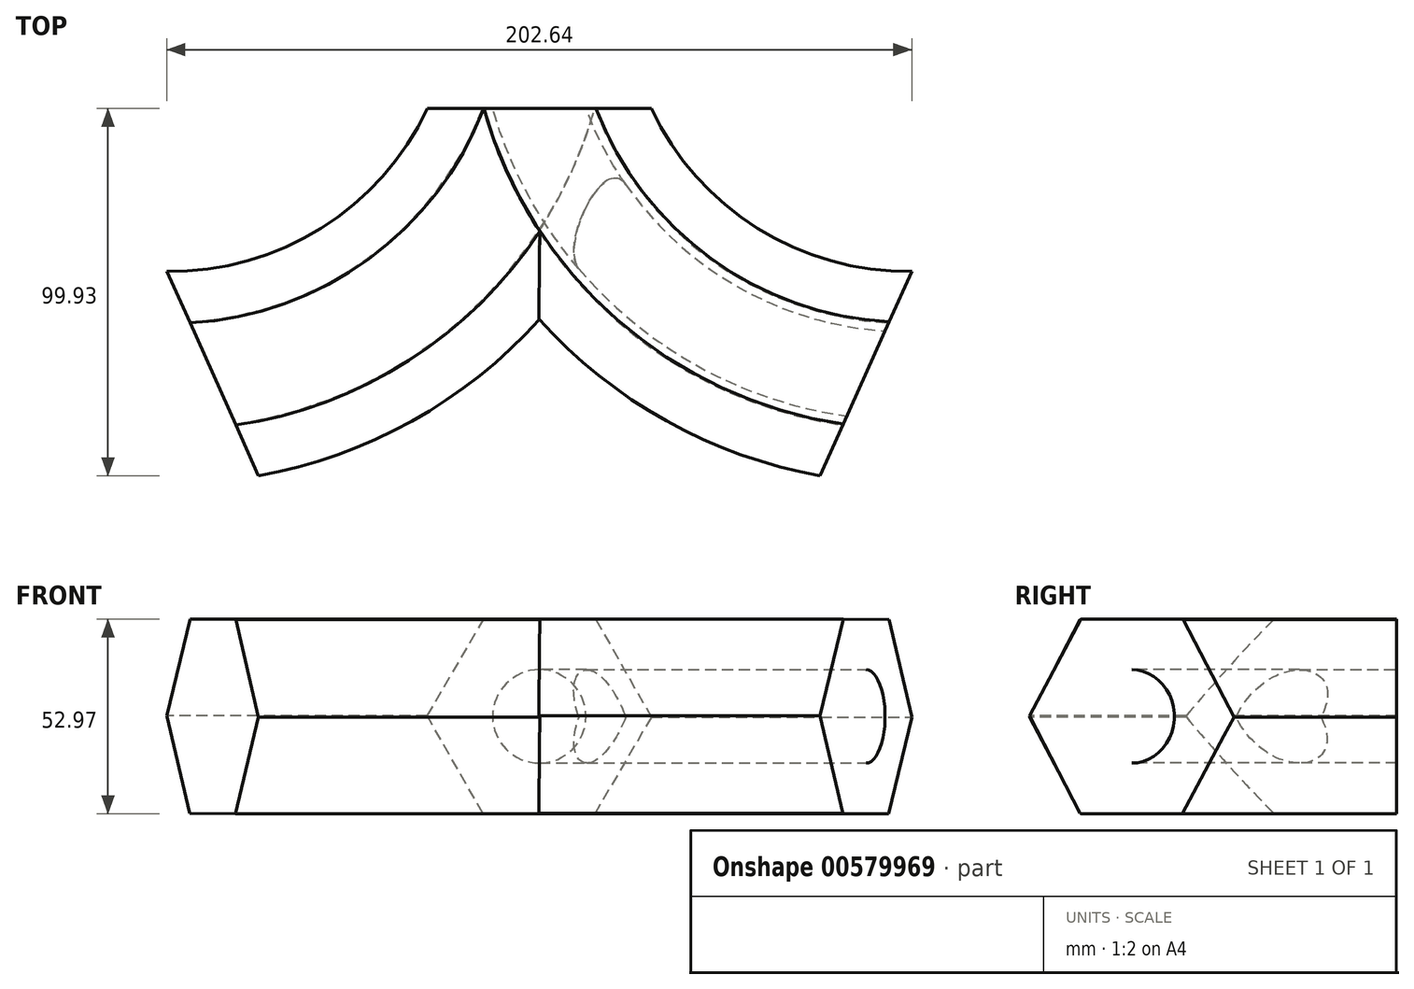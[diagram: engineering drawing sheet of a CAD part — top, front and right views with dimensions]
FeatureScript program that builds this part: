
annotation { "Feature Type Name" : "Feature", "Feature Type Description" : "" }
export const myFeature = defineFeature(function(context is Context, id is Id, definition is map)
    precondition{}
    {
        {
            var Q0;
            Q0=qCreatedBy(makeId("Front.planeOp"),FACE);
            var sketch = newSketch(context, id + "F0", { "sketchPlane" : qUnion([Q0])});
            skCircle(sketch, "E0.cCircle", {"center": v(0, 26.89) * mm, "radius": 26.4 * mm, "construction": true});
            skLineSegment(sketch, "E0.0", {"start": v(-15.4, 0.58) * mm, "end": v(-30.48, 27.07) * mm});
            skLineSegment(sketch, "E0.1", {"start": v(-30.48, 27.07) * mm, "end": v(-15.08, 53.37) * mm});
            skLineSegment(sketch, "E0.2", {"start": v(-15.08, 53.37) * mm, "end": v(15.4, 53.2) * mm});
            skLineSegment(sketch, "E0.3", {"start": v(15.4, 53.2) * mm, "end": v(30.48, 26.7) * mm});
            skLineSegment(sketch, "E0.4", {"start": v(30.48, 26.7) * mm, "end": v(15.08, 0.4) * mm});
            skLineSegment(sketch, "E0.5", {"start": v(15.08, 0.4) * mm, "end": v(-15.4, 0.58) * mm});
            skPoint(sketch, "E0.0.midPoint", {"position": v(-22.94, 13.82) * mm});
            skCircle(sketch, "E1", {"center": v(0, 26.89) * mm, "radius": 12.7 * mm});
            skSolve(sketch);
        }
        {
            var Q0;
            Q0=qCreatedBy(makeId("Top.planeOp"),FACE);
            var sketch = newSketch(context, id + "F1", { "sketchPlane" : qUnion([Q0])});
            skArc(sketch, "E2", {"start": v(-88.86, -72.11) * mm, "mid": v(-33.77, -49.2) * mm, "end": v(0, 0) * mm});
            skArc(sketch, "E3.MirrorCS", {"start": v(88.86, -72.11) * mm, "mid": v(33.77, -49.2) * mm, "end": v(0, 0) * mm});
            skSolve(sketch);
        }
        {
            var Q0;
            Q0=makeQuery(id+"F0.imprint","IMPRINT",FACE,{"disambiguationData":[TD([[makeQuery(id+"F0.imprint","IMPRINT",EDGE,{"derivedFrom":sQuery(id+"F0.wireOp",EDGE,"E0.0")}),-1.0]])]});
            var Q1;
            Q1=makeQuery(id+"F0.imprint","IMPRINT",FACE,{"disambiguationData":[TD([[makeQuery(id+"F0.imprint","IMPRINT",EDGE,{"derivedFrom":sQuery(id+"F0.wireOp",EDGE,"E1")}),1.0]])]});
            var Q2;
            Q2=sQuery(id+"F1.wireOp",EDGE,"E2");
            sweep(context, id + "F2", {"profiles" : qUnion([Q0, Q1]), "path" : qUnion([Q2])});
        }
        {
            var Q0;
            Q0=makeQuery(id+"F0.imprint","IMPRINT",FACE,{"disambiguationData":[TD([[makeQuery(id+"F0.imprint","IMPRINT",EDGE,{"derivedFrom":sQuery(id+"F0.wireOp",EDGE,"E0.0")}),-1.0]])]});
            var Q1;
            Q1=sQuery(id+"F1.wireOp",EDGE,"E3.MirrorCS");
            sweep(context, id + "F3", {"operationType" : NewBodyOperationType.ADD, "profiles" : qUnion([Q0]), "path" : qUnion([Q1])});
        }
        {
            var Q0;
            Q0=makeQuery(id+"F0.imprint","IMPRINT",FACE,{"disambiguationData":[TD([[makeQuery(id+"F0.imprint","IMPRINT",EDGE,{"derivedFrom":sQuery(id+"F0.wireOp",EDGE,"E1")}),1.0]])]});
            var Q1;
            Q1=sQuery(id+"F1.wireOp",EDGE,"E3.MirrorCS");
            sweep(context, id + "F4", {"operationType" : NewBodyOperationType.REMOVE, "profiles" : qUnion([Q0]), "path" : qUnion([Q1])});
        }
    });
